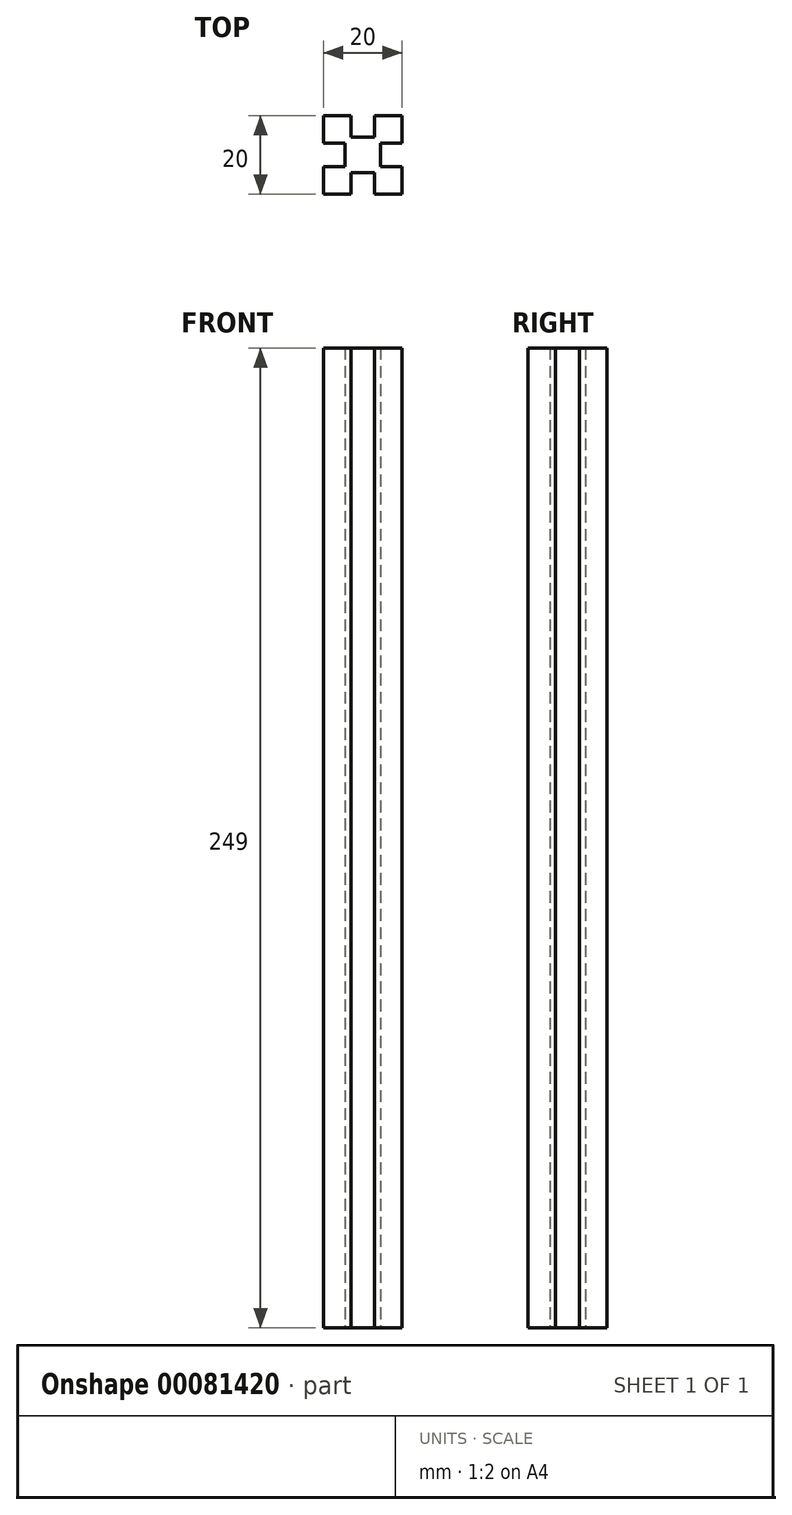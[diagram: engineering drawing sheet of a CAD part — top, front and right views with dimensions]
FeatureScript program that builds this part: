
annotation { "Feature Type Name" : "Feature", "Feature Type Description" : "" }
export const myFeature = defineFeature(function(context is Context, id is Id, definition is map)
    precondition{}
    {
        {
            var Q0;
            Q0=qCreatedBy(makeId("Top.planeOp"),FACE);
            var sketch = newSketch(context, id + "F0", { "sketchPlane" : qUnion([Q0])});
            skLineSegment(sketch, "E0.bottom", {"start": v(-87.17, -55.96) * mm, "end": v(-67.17, -55.96) * mm});
            skLineSegment(sketch, "E0.top", {"start": v(-87.17, -35.96) * mm, "end": v(-67.17, -35.96) * mm});
            skLineSegment(sketch, "E0.left", {"start": v(-87.17, -55.96) * mm, "end": v(-87.17, -35.96) * mm});
            skLineSegment(sketch, "E0.right", {"start": v(-67.17, -55.96) * mm, "end": v(-67.17, -35.96) * mm});
            skLineSegment(sketch, "E1.bottom", {"start": v(-80.17, -35.96) * mm, "end": v(-74.17, -35.96) * mm});
            skLineSegment(sketch, "E1.top", {"start": v(-80.17, -41.46) * mm, "end": v(-74.17, -41.46) * mm});
            skLineSegment(sketch, "E1.left", {"start": v(-80.17, -35.96) * mm, "end": v(-80.17, -41.46) * mm});
            skLineSegment(sketch, "E1.right", {"start": v(-74.17, -35.96) * mm, "end": v(-74.17, -41.46) * mm});
            skLineSegment(sketch, "E2.bottom", {"start": v(-67.17, -42.96) * mm, "end": v(-72.67, -42.96) * mm});
            skLineSegment(sketch, "E2.top", {"start": v(-67.17, -48.96) * mm, "end": v(-72.67, -48.96) * mm});
            skLineSegment(sketch, "E2.left", {"start": v(-67.17, -42.96) * mm, "end": v(-67.17, -48.96) * mm});
            skLineSegment(sketch, "E2.right", {"start": v(-72.67, -42.96) * mm, "end": v(-72.67, -48.96) * mm});
            skLineSegment(sketch, "E3.bottom", {"start": v(-74.17, -55.96) * mm, "end": v(-80.17, -55.96) * mm});
            skLineSegment(sketch, "E3.top", {"start": v(-74.17, -50.46) * mm, "end": v(-80.17, -50.46) * mm});
            skLineSegment(sketch, "E3.left", {"start": v(-74.17, -55.96) * mm, "end": v(-74.17, -50.46) * mm});
            skLineSegment(sketch, "E3.right", {"start": v(-80.17, -55.96) * mm, "end": v(-80.17, -50.46) * mm});
            skLineSegment(sketch, "E4.bottom", {"start": v(-87.17, -48.96) * mm, "end": v(-81.67, -48.96) * mm});
            skLineSegment(sketch, "E4.top", {"start": v(-87.17, -42.96) * mm, "end": v(-81.67, -42.96) * mm});
            skLineSegment(sketch, "E4.left", {"start": v(-87.17, -48.96) * mm, "end": v(-87.17, -42.96) * mm});
            skLineSegment(sketch, "E4.right", {"start": v(-81.67, -48.96) * mm, "end": v(-81.67, -42.96) * mm});
            skSolve(sketch);
        }
        {
            var Q0;
            Q0=makeQuery(id+"F0.imprint","IMPRINT",FACE,{"disambiguationData":[TD([[makeQuery(id+"F0.imprint","IMPRINT",EDGE,{"derivedFrom":sQuery(id+"F0.wireOp",EDGE,"E1.top")}),-1.0]])]});
            extrude(context, id + "F1", {"entities" : qUnion([Q0]), "depth" : 249 * mm});
        }
    });
